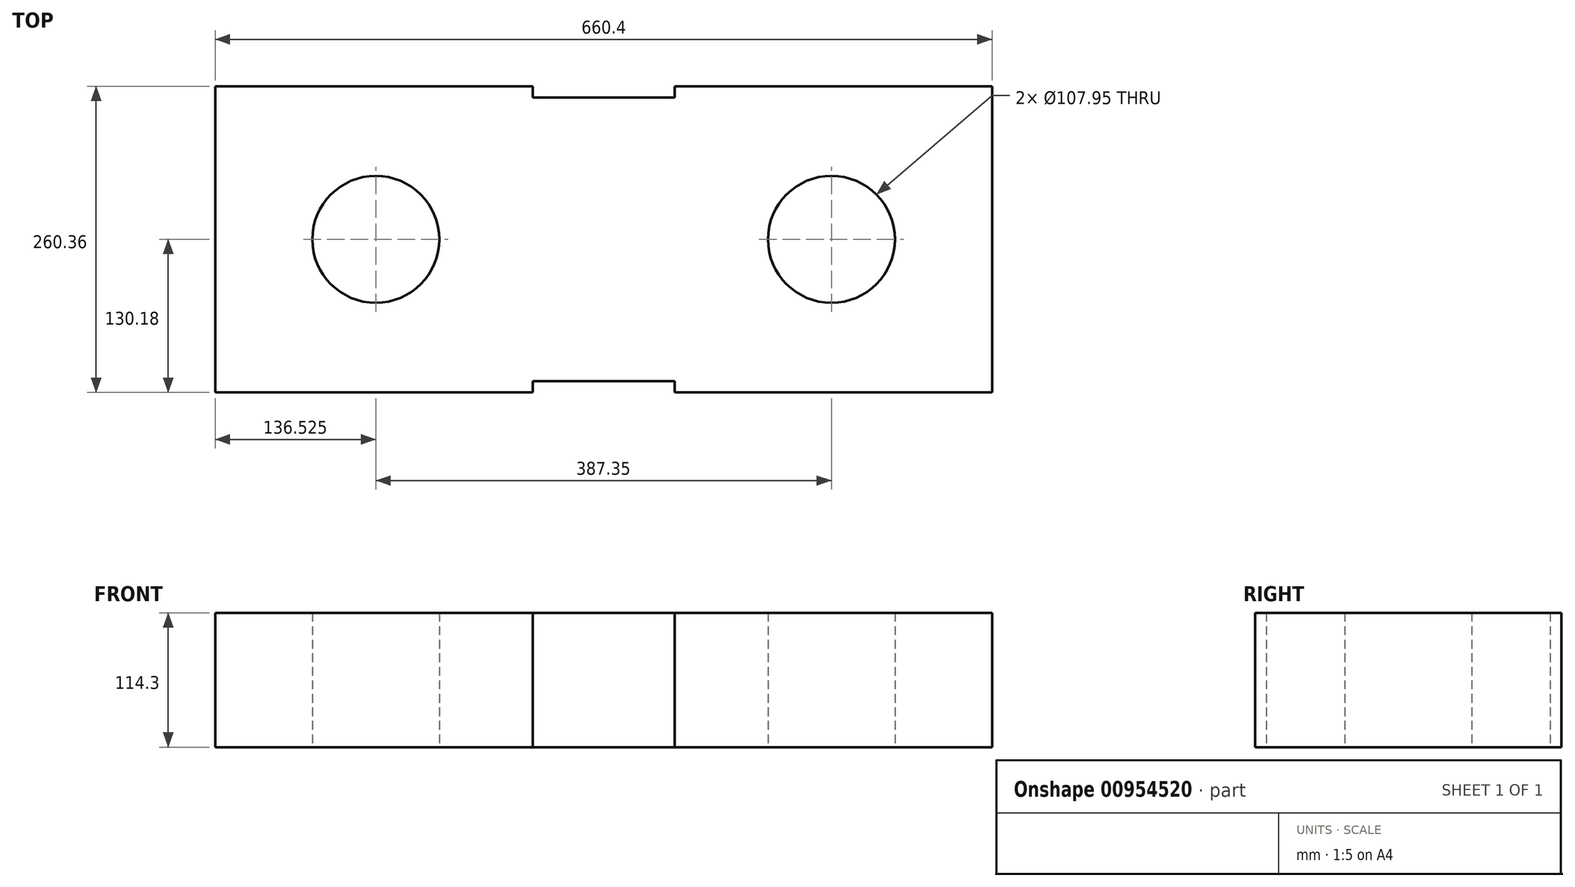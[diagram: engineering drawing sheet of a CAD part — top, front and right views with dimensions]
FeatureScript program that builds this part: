
annotation { "Feature Type Name" : "Feature", "Feature Type Description" : "" }
export const myFeature = defineFeature(function(context is Context, id is Id, definition is map)
    precondition{}
    {
        {
            var Q0;
            Q0=qCreatedBy(makeId("Top.planeOp"),FACE);
            var sketch = newSketch(context, id + "F0", { "sketchPlane" : qUnion([Q0])});
            skLineSegment(sketch, "E0.bottom", {"start": v(330.2, 130.18) * mm, "end": v(60.33, 130.18) * mm});
            skLineSegment(sketch, "E0.top", {"start": v(330.2, -130.18) * mm, "end": v(60.33, -130.18) * mm});
            skLineSegment(sketch, "E0.left", {"start": v(330.2, 130.18) * mm, "end": v(330.2, -130.18) * mm});
            skLineSegment(sketch, "E0.right", {"start": v(-330.2, 130.18) * mm, "end": v(-330.2, -130.18) * mm});
            skPoint(sketch, "E0.middle", {"position": v(0, 0) * mm});
            skCircle(sketch, "E1", {"center": v(-193.68, 0) * mm, "radius": 53.98 * mm});
            skLineSegment(sketch, "E2", {"start": v(0, 130.18) * mm, "end": v(0, -130.18) * mm, "construction": true});
            skCircle(sketch, "E3.MirrorC", {"center": v(193.68, 0) * mm, "radius": 53.98 * mm});
            skLineSegment(sketch, "E4.0", {"start": v(60.33, 130.18) * mm, "end": v(60.33, 120.65) * mm});
            skLineSegment(sketch, "E5.MirrorCS", {"start": v(-60.33, 130.18) * mm, "end": v(-60.33, 120.65) * mm});
            skLineSegment(sketch, "E6.0", {"start": v(60.33, 120.65) * mm, "end": v(-60.33, 120.65) * mm});
            skLineSegment(sketch, "E6.2", {"start": v(60.33, -120.65) * mm, "end": v(-60.33, -120.65) * mm});
            skLineSegment(sketch, "E7.trimOffspring", {"start": v(-60.32, -120.65) * mm, "end": v(-60.32, -130.18) * mm});
            skLineSegment(sketch, "E8.trimOffspring", {"start": v(60.32, -120.65) * mm, "end": v(60.32, -130.18) * mm});
            skLineSegment(sketch, "E9.trimOffspring", {"start": v(-60.33, 130.18) * mm, "end": v(-330.2, 130.18) * mm});
            skLineSegment(sketch, "E10.trimOffspring", {"start": v(-60.33, -130.18) * mm, "end": v(-330.2, -130.18) * mm});
            skSolve(sketch);
        }
        {
            var Q0;
            Q0=makeQuery(id+"F0.imprint","IMPRINT",FACE,{"disambiguationData":[TD([[makeQuery(id+"F0.imprint","IMPRINT",EDGE,{"derivedFrom":sQuery(id+"F0.wireOp",EDGE,"E0.bottom")}),1.0]])]});
            extrude(context, id + "F1", {"entities" : qUnion([Q0]), "depth" : 114.3 * mm, "offsetDistance" : 25.4 * mm});
        }
    });
